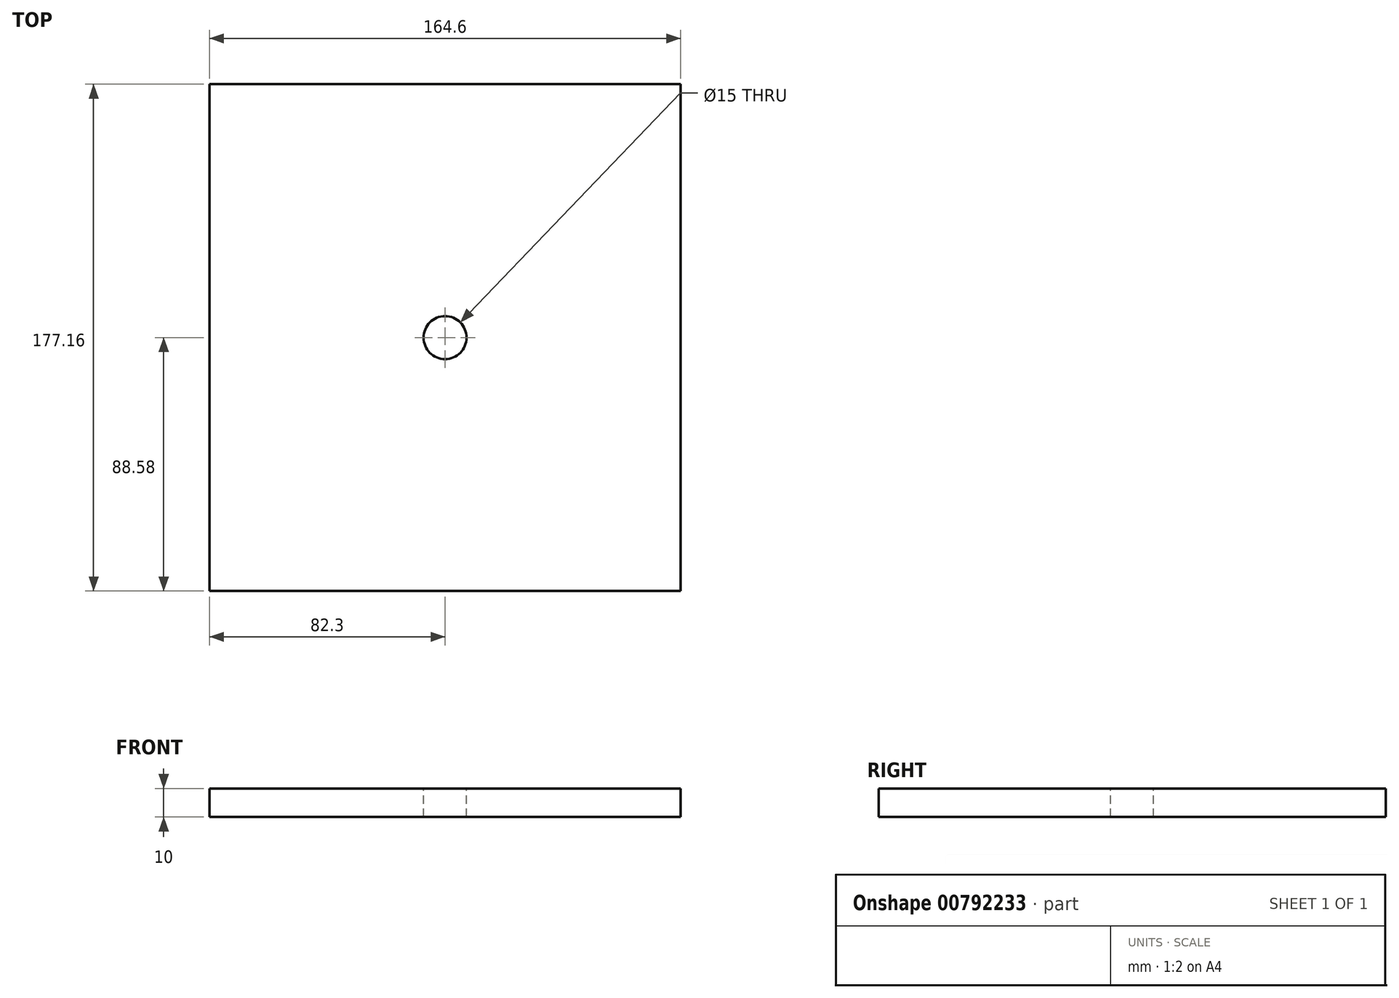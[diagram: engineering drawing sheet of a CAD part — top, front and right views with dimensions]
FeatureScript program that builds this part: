
annotation { "Feature Type Name" : "Feature", "Feature Type Description" : "" }
export const myFeature = defineFeature(function(context is Context, id is Id, definition is map)
    precondition{}
    {
        {
            var Q0;
            Q0=qCreatedBy(makeId("Top.planeOp"),FACE);
            var sketch = newSketch(context, id + "F0", { "sketchPlane" : qUnion([Q0])});
            skLineSegment(sketch, "E0.bottom", {"start": v(82.3, 88.58) * mm, "end": v(-82.3, 88.58) * mm});
            skLineSegment(sketch, "E0.top", {"start": v(82.3, -88.58) * mm, "end": v(-82.3, -88.58) * mm});
            skLineSegment(sketch, "E0.left", {"start": v(82.3, 88.58) * mm, "end": v(82.3, -88.58) * mm});
            skLineSegment(sketch, "E0.right", {"start": v(-82.3, 88.58) * mm, "end": v(-82.3, -88.58) * mm});
            skPoint(sketch, "E0.middle", {"position": v(0, 0) * mm});
            skSolve(sketch);
        }
        {
            var Q0;
            Q0=makeQuery(id+"F0.imprint","IMPRINT",FACE,{"disambiguationData":[TD([[makeQuery(id+"F0.imprint","IMPRINT",EDGE,{"derivedFrom":sQuery(id+"F0.wireOp",EDGE,"E0.bottom")}),1.0]])]});
            extrude(context, id + "F1", {"entities" : qUnion([Q0]), "depth" : 10 * mm, "offsetDistance" : 25 * mm});
        }
        {
            var Q0;
            Q0=makeQuery(id+"F1.opExtrude","CAP_FACE",FACE,{"disambiguationData":[OSD([sQuery(id+"F0.wireOp",EDGE,"E0.bottom"),sQuery(id+"F0.wireOp",EDGE,"E0.top"),sQuery(id+"F0.wireOp",EDGE,"E0.left"),sQuery(id+"F0.wireOp",EDGE,"E0.right")])],"isStart":false});
            var sketch = newSketch(context, id + "F2", { "sketchPlane" : qUnion([Q0])});
            skCircle(sketch, "E1", {"center": v(0, 0) * mm, "radius": 9.64 * mm});
            skSolve(sketch);
        }
        {
            var Q0;
            Q0=sQuery(id+"F2.wireOp",VERTEX,"E1.center");
            var Q1;
            Q1=makeQuery(id+"F1.opExtrude","SWEPT_BODY",BODY,{"disambiguationData":[OSD([sQuery(id+"F0.wireOp",EDGE,"E0.bottom"),sQuery(id+"F0.wireOp",EDGE,"E0.top"),sQuery(id+"F0.wireOp",EDGE,"E0.left"),sQuery(id+"F0.wireOp",EDGE,"E0.right")])]});
            hole(context, id + "F3", {"style" : HoleStyle.SIMPLE, "endStyle" : HoleEndStyle.THROUGH, "holeDiameter" : 15 * mm, "majorDiameter" : 5 * mm, "isTappedThrough" : true, "tappedDepth" : 12 * mm, "tapClearance" : 3, "locations" : qUnion([Q0]), "scope" : qUnion([Q1])});
        }
    });
